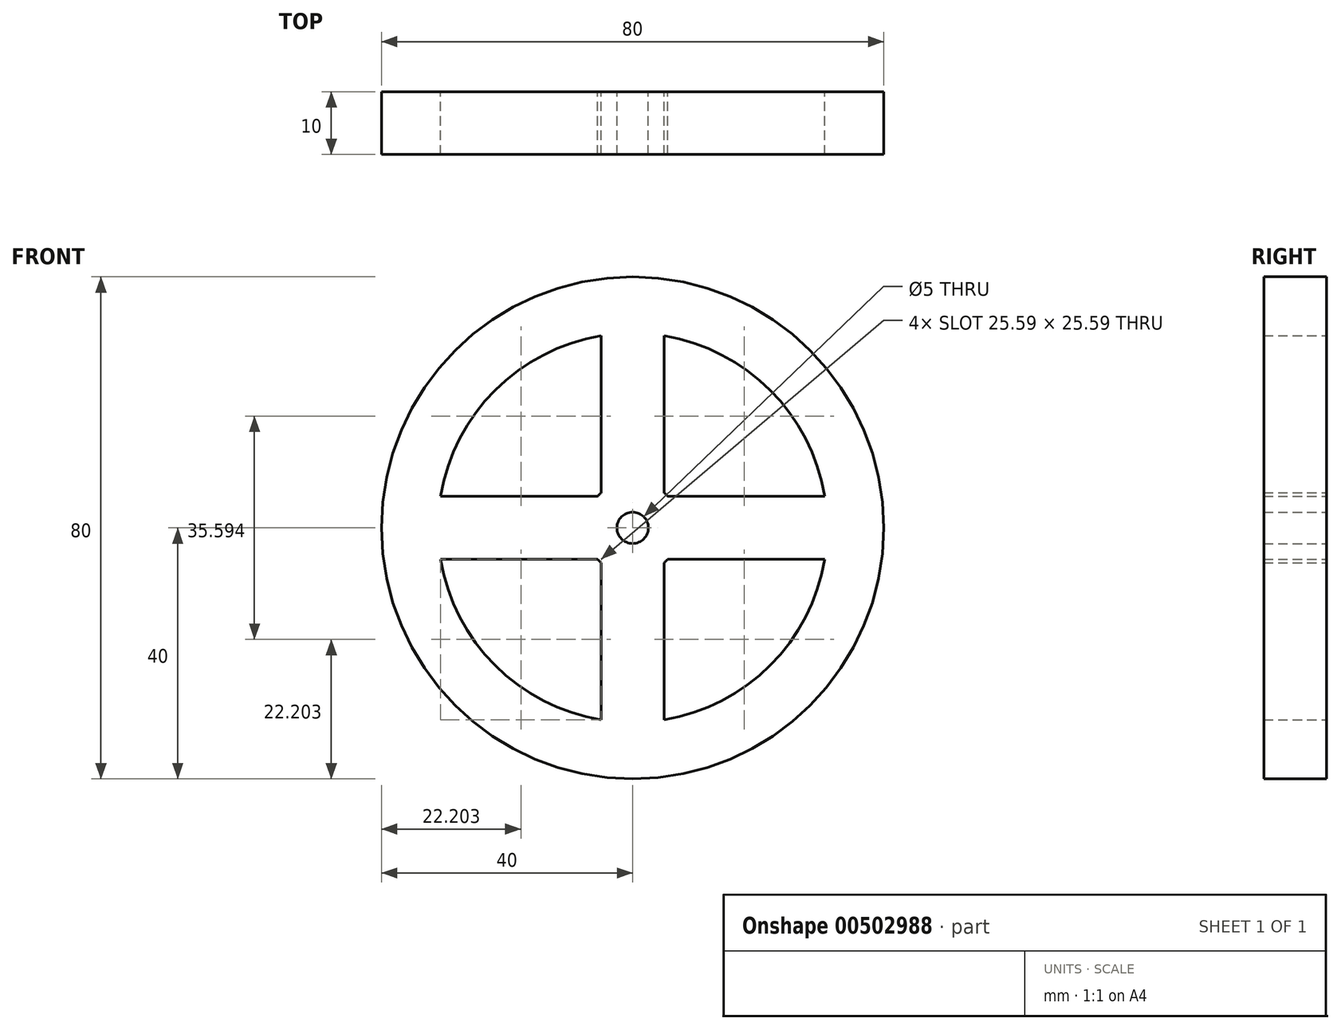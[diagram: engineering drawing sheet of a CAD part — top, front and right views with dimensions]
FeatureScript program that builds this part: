
annotation { "Feature Type Name" : "Feature", "Feature Type Description" : "" }
export const myFeature = defineFeature(function(context is Context, id is Id, definition is map)
    precondition{}
    {
        {
            var Q0;
            Q0=qCreatedBy(makeId("Front.planeOp"),FACE);
            var sketch = newSketch(context, id + "F0", { "sketchPlane" : qUnion([Q0])});
            skCircle(sketch, "E0", {"center": v(0, 0) * mm, "radius": 40 * mm});
            skArc(sketch, "E1", {"start": v(-30.6, -5) * mm, "mid": v(-21.92, -21.92) * mm, "end": v(-5, -30.6) * mm});
            skArc(sketch, "E2", {"start": v(5.6, 5) * mm, "mid": v(5.3, 5.3) * mm, "end": v(5, 5.6) * mm});
            skCircle(sketch, "E3", {"center": v(0, 0) * mm, "radius": 2.5 * mm});
            skLineSegment(sketch, "E4.0", {"start": v(5, 5.6) * mm, "end": v(5, 30.6) * mm});
            skLineSegment(sketch, "E5.0", {"start": v(-5, 5.6) * mm, "end": v(-5, 30.6) * mm});
            skLineSegment(sketch, "E6.0", {"start": v(-5.6, 5) * mm, "end": v(-30.6, 5) * mm});
            skLineSegment(sketch, "E7.0", {"start": v(-5.6, -5) * mm, "end": v(-30.6, -5) * mm});
            skLineSegment(sketch, "E8.0", {"start": v(-5, -5.6) * mm, "end": v(-5, -30.6) * mm});
            skLineSegment(sketch, "E9.0", {"start": v(5, -5.6) * mm, "end": v(5, -30.6) * mm});
            skLineSegment(sketch, "E10.0", {"start": v(5.6, -5) * mm, "end": v(30.6, -5) * mm});
            skLineSegment(sketch, "E11.0", {"start": v(5.6, 5) * mm, "end": v(30.6, 5) * mm});
            skLineSegment(sketch, "E12.trimOffspring", {"start": v(-5, 39.69) * mm, "end": v(-5, 40) * mm});
            skLineSegment(sketch, "E13.trimOffspring", {"start": v(39.69, 5) * mm, "end": v(40, 5) * mm});
            skLineSegment(sketch, "E14.trimOffspring", {"start": v(39.69, -5) * mm, "end": v(40, -5) * mm});
            skLineSegment(sketch, "E15.trimOffspring", {"start": v(-39.69, -5) * mm, "end": v(-40, -5) * mm});
            skLineSegment(sketch, "E16.trimOffspring", {"start": v(-39.69, 5) * mm, "end": v(-40, 5) * mm});
            skLineSegment(sketch, "E17.trimOffspring", {"start": v(5, 39.69) * mm, "end": v(5, 40) * mm});
            skLineSegment(sketch, "E18.trimOffspring", {"start": v(5, -39.69) * mm, "end": v(5, -40) * mm});
            skLineSegment(sketch, "E19.trimOffspring", {"start": v(-5, -39.69) * mm, "end": v(-5, -40) * mm});
            skArc(sketch, "E20.trimOffspring", {"start": v(-5, 5.6) * mm, "mid": v(-5.3, 5.3) * mm, "end": v(-5.6, 5) * mm});
            skArc(sketch, "E21.trimOffspring", {"start": v(-5.6, -5) * mm, "mid": v(-5.3, -5.3) * mm, "end": v(-5, -5.6) * mm});
            skArc(sketch, "E22.trimOffspring", {"start": v(5, -5.6) * mm, "mid": v(5.3, -5.3) * mm, "end": v(5.6, -5) * mm});
            skArc(sketch, "E23.trimOffspring", {"start": v(30.6, 5) * mm, "mid": v(21.92, 21.92) * mm, "end": v(5, 30.6) * mm});
            skArc(sketch, "E24.trimOffspring", {"start": v(-5, 30.6) * mm, "mid": v(-21.92, 21.92) * mm, "end": v(-30.6, 5) * mm});
            skArc(sketch, "E25.trimOffspring", {"start": v(5, -30.6) * mm, "mid": v(21.92, -21.92) * mm, "end": v(30.6, -5) * mm});
            skSolve(sketch);
        }
        {
            var Q0;
            Q0=makeQuery(id+"F0.imprint","IMPRINT",FACE,{"disambiguationData":[TD([[makeQuery(id+"F0.imprint","IMPRINT",EDGE,{"derivedFrom":sQuery(id+"F0.wireOp",EDGE,"E1")}),-1.0]])]});
            extrude(context, id + "F1", {"entities" : qUnion([Q0]), "depth" : 10 * mm, "offsetDistance" : 25 * mm});
        }
    });
